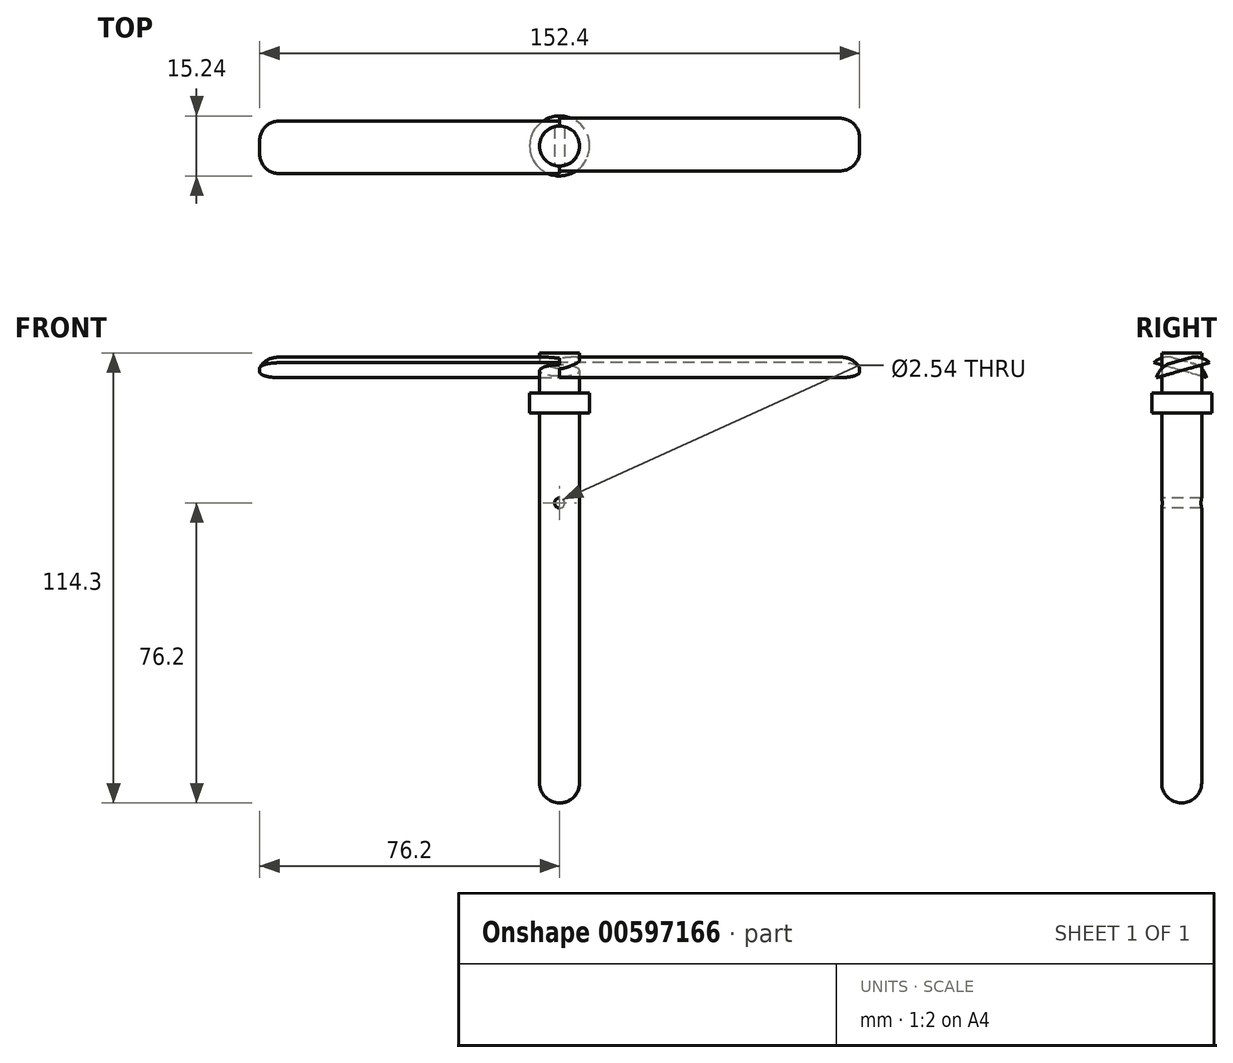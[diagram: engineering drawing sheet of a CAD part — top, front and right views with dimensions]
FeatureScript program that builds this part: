
annotation { "Feature Type Name" : "Feature", "Feature Type Description" : "" }
export const myFeature = defineFeature(function(context is Context, id is Id, definition is map)
    precondition{}
    {
        {
            var Q0;
            Q0=qCreatedBy(makeId("Top.planeOp"),FACE);
            var sketch = newSketch(context, id + "F0", { "sketchPlane" : qUnion([Q0])});
            skCircle(sketch, "E0", {"center": v(0, 0) * mm, "radius": 5.08 * mm});
            skSolve(sketch);
        }
        {
            var Q0;
            Q0=makeQuery(id+"F0.imprint","IMPRINT",FACE,{"disambiguationData":[TD([[makeQuery(id+"F0.imprint","IMPRINT",EDGE,{"derivedFrom":sQuery(id+"F0.wireOp",EDGE,"E0")}),1.0]])]});
            extrude(context, id + "F1", {"entities" : qUnion([Q0]), "depth" : 76.2 * mm, "offsetDistance" : 25.4 * mm});
        }
        {
            var Q0;
            Q0=qCreatedBy(makeId("Right.planeOp"),FACE);
            var sketch = newSketch(context, id + "F2", { "sketchPlane" : qUnion([Q0])});
            skLineSegment(sketch, "E1", {"start": v(6.35, 76.2) * mm, "end": v(-7.04, 72.39) * mm});
            skLineSegment(sketch, "E2", {"start": v(-7.04, 72.4) * mm, "end": v(-6.35, 69.95) * mm});
            skLineSegment(sketch, "E3", {"start": v(-6.35, 69.95) * mm, "end": v(7.04, 73.76) * mm});
            skLineSegment(sketch, "E4", {"start": v(7.04, 73.76) * mm, "end": v(6.35, 76.2) * mm});
            skLineSegment(sketch, "E5", {"start": v(0, 0) * mm, "end": v(0, 80.68) * mm, "construction": true});
            skSolve(sketch);
        }
        {
            var Q0;
            Q0=makeQuery(id+"F2.imprint","IMPRINT",FACE,{"disambiguationData":[TD([[makeQuery(id+"F2.imprint","IMPRINT",EDGE,{"derivedFrom":sQuery(id+"F2.wireOp",EDGE,"E1")}),1.0]])]});
            extrude(context, id + "F3", {"entities" : qUnion([Q0]), "operationType" : NewBodyOperationType.ADD, "depth" : 76.2 * mm, "offsetDistance" : 25.4 * mm});
        }
        {
            var Q0;
            Q0=makeQuery(id+"F1.opExtrude","SWEPT_BODY",BODY,{"disambiguationData":[OSD([sQuery(id+"F0.wireOp",EDGE,"E0")])]});
            var Q1;
            Q1=makeQuery(id+"F1.opExtrude","SWEPT_FACE",FACE,{"disambiguationData":[OSD([sQuery(id+"F0.wireOp",EDGE,"E0")])]});
            circularPattern(context, id + "F4", {"operationType" : NewBodyOperationType.ADD, "entities" : qUnion([Q0]), "axis" : qUnion([Q1]), "angle" : 360 * degree, "instanceCount" : 2, "equalSpace" : true, "isCentered" : true});
        }
        {
            var Q0;
            Q0=qCreatedBy(makeId("Front.planeOp"),FACE);
            var sketch = newSketch(context, id + "F5", { "sketchPlane" : qUnion([Q0])});
            skLineSegment(sketch, "E6", {"start": v(0, 0) * mm, "end": v(0, 109.6) * mm, "construction": true});
            skSolve(sketch);
        }
        {
            var Q0;
            Q0=makeQuery(id+"F3.opExtrude","CAP_EDGE",EDGE,{"disambiguationData":[OSD([sQuery(id+"F2.wireOp",EDGE,"E4")])],"isStart":false});
            var Q1;
            Q1=makeQuery(id+"F3.opExtrude","CAP_EDGE",EDGE,{"disambiguationData":[OSD([sQuery(id+"F2.wireOp",EDGE,"E2")])],"isStart":false});
            var Q2;
            Q2=makeQuery(id+"F4.opPattern","COPY",EDGE,{"derivedFrom":makeQuery(id+"F3.opExtrude","CAP_EDGE",EDGE,{"disambiguationData":[OSD([sQuery(id+"F2.wireOp",EDGE,"E4")])],"isStart":false}),"instanceName":"-1"});
            var Q3;
            Q3=makeQuery(id+"F4.opPattern","COPY",EDGE,{"derivedFrom":makeQuery(id+"F3.opExtrude","CAP_EDGE",EDGE,{"disambiguationData":[OSD([sQuery(id+"F2.wireOp",EDGE,"E2")])],"isStart":false}),"instanceName":"-1"});
            fillet(context, id + "F6", {"entities" : qUnion([Q0, Q1, Q2, Q3]), "radius" : 5.08 * mm, "tangentPropagation" : true, "allowEdgeOverflow" : false});
        }
        {
            var Q0;
            Q0=qCreatedBy(makeId("Front.planeOp"),FACE);
            var sketch = newSketch(context, id + "F7", { "sketchPlane" : qUnion([Q0])});
            skCircle(sketch, "E7", {"center": v(0, 38.1) * mm, "radius": 1.27 * mm});
            skSolve(sketch);
        }
        {
            var Q0;
            Q0 = qSketchRegion(id + "F7", true);
            extrude(context, id + "F8", {"entities" : qUnion([Q0]), "operationType" : NewBodyOperationType.REMOVE, "endBound" : BoundingType.THROUGH_ALL, "oppositeDirection" : true, "depth" : 101.6 * mm, "offsetDistance" : 25.4 * mm});
        }
        {
            var Q0;
            Q0=makeQuery(id+"F8.boolean.opBoolean","COPY",FACE,{"derivedFrom":makeQuery(id+"F8.opExtrude","CAP_FACE",FACE,{"disambiguationData":[OSD([sQuery(id+"F7.wireOp",EDGE,"E7")])],"isStart":true})});
            extrude(context, id + "F9", {"entities" : qUnion([Q0]), "operationType" : NewBodyOperationType.REMOVE, "oppositeDirection" : true, "depth" : 25.4 * mm, "offsetDistance" : 25.4 * mm});
        }
        {
            var Q0;
            Q0=makeQuery(id+"F4.opPattern","COPY",EDGE,{"derivedFrom":makeQuery(id+"F3.opExtrude","SWEPT_EDGE",EDGE,{"disambiguationData":[OSD([sQuery(id+"F2.wireOp",EDGE,"E1"),sQuery(id+"F2.wireOp",EDGE,"E4")])]}),"instanceName":"-1"});
            var Q1;
            Q1=makeQuery(id+"F3.opExtrude","SWEPT_EDGE",EDGE,{"disambiguationData":[OSD([sQuery(id+"F2.wireOp",EDGE,"E1"),sQuery(id+"F2.wireOp",EDGE,"E4")])]});
            fillet(context, id + "F10", {"entities" : qUnion([Q0, Q1]), "radius" : 5.08 * mm, "tangentPropagation" : true, "allowEdgeOverflow" : false});
        }
        {
            var Q0;
            Q0=makeQuery(id+"F1.opExtrude","CAP_FACE",FACE,{"disambiguationData":[OSD([sQuery(id+"F0.wireOp",EDGE,"E0")])],"isStart":true});
            extrude(context, id + "F11", {"entities" : qUnion([Q0]), "operationType" : NewBodyOperationType.ADD, "depth" : 38.1 * mm, "offsetDistance" : 25.4 * mm});
        }
        {
            var Q0;
            Q0=makeQuery(id+"F11.opExtrude","CAP_EDGE",EDGE,{"disambiguationData":[OSD([sQuery(id+"F0.wireOp",EDGE,"E0")])],"isStart":false});
            fillet(context, id + "F12", {"entities" : qUnion([Q0]), "radius" : 5.08 * mm, "tangentPropagation" : true, "allowEdgeOverflow" : false});
        }
        {
            var Q0;
            Q0=qCreatedBy(makeId("Top.planeOp"),FACE);
            cPlane(context, id + "F13", {"entities" : qUnion([Q0]), "cplaneType" : CPlaneType.OFFSET, "offset" : 66.04 * mm, "width" : 152.4 * mm, "height" : 152.4 * mm});
        }
        {
            var Q0;
            Q0=qCreatedBy(id+"F13.planeOp",FACE);
            var sketch = newSketch(context, id + "F14", { "sketchPlane" : qUnion([Q0])});
            skCircle(sketch, "E8", {"center": v(0, 0) * mm, "radius": 7.62 * mm});
            skSolve(sketch);
        }
        {
            var Q0;
            Q0=makeQuery(id+"F14.imprint","IMPRINT",FACE,{"disambiguationData":[TD([[makeQuery(id+"F14.imprint","IMPRINT",EDGE,{"derivedFrom":sQuery(id+"F14.wireOp",EDGE,"E8")}),1.0]])]});
            extrude(context, id + "F15", {"entities" : qUnion([Q0]), "operationType" : NewBodyOperationType.ADD, "oppositeDirection" : true, "depth" : 5.08 * mm, "offsetDistance" : 25.4 * mm});
        }
    });
